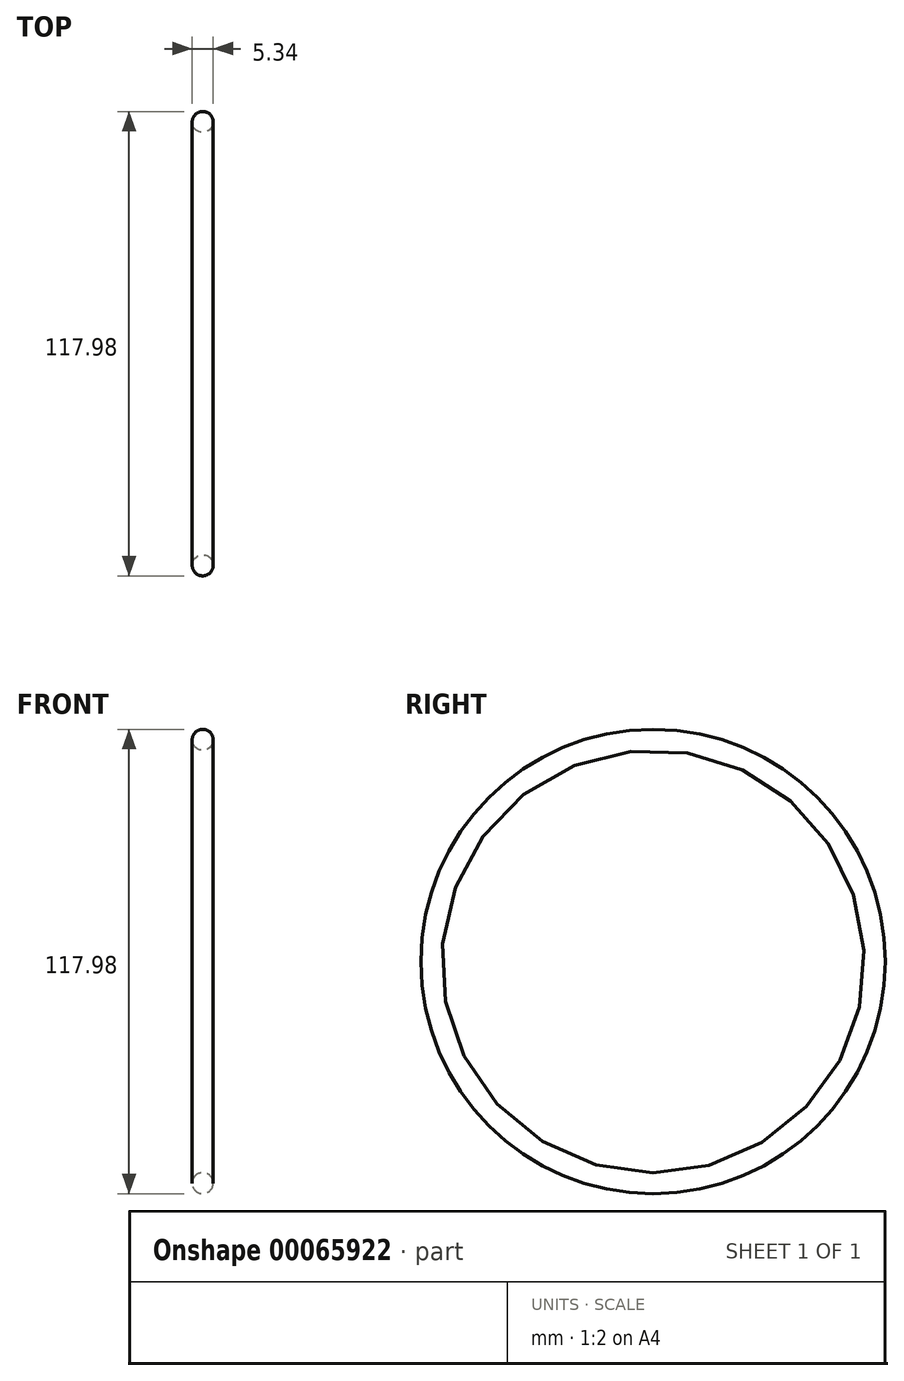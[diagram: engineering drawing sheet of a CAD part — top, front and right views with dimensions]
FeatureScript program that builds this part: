
annotation { "Feature Type Name" : "Feature", "Feature Type Description" : "" }
export const myFeature = defineFeature(function(context is Context, id is Id, definition is map)
    precondition{}
    {
        {
            var Q0;
            Q0=qCreatedBy(makeId("Front.planeOp"),FACE);
            var sketch = newSketch(context, id + "F0", { "sketchPlane" : qUnion([Q0])});
            skLineSegment(sketch, "E0", {"start": v(0, 0) * mm, "end": v(-6.06, 0) * mm, "construction": true});
            skCircle(sketch, "E1", {"center": v(0, 56.32) * mm, "radius": 2.67 * mm});
            skSolve(sketch);
        }
        {
            var Q0;
            Q0=makeQuery(id+"F0.imprint","IMPRINT",FACE,{"disambiguationData":[TD([[makeQuery(id+"F0.imprint","IMPRINT",EDGE,{"derivedFrom":sQuery(id+"F0.wireOp",EDGE,"E1")}),1.0]])]});
            var Q1;
            Q1=sQuery(id+"F0.wireOp",EDGE,"E0");
            revolve(context, id + "F1", {"entities" : qUnion([Q0]), "axis" : qUnion([Q1]), "revolveType" : RevolveType.FULL});
        }
    });
